# Revit family: M06
name_source: partatom
category: Verbindungsmittel
units: mm (PartAtom-declared; Revit-internal decimal feet)

## family parameters
Arbeitsebenenbasiert = Nein
Beim Laden mit Abzugskörper schneiden = Nein
Gemeinsam genutzt = Nein
Immer vertikal = Nein
OmniClass-Nummer = 23.25.10.27.11.21
OmniClass-Titel = Reinforcement Couplers

## types (10) — shared parameters
Endenbearbeitung 1 = Mit Gewinde
Endenbearbeitung 2 = Mit Gewinde
Hersteller = Stahlwerk Annahütte Max Aicher GmbH Co.KG
M06_Vis = Ja
SW Winkel = 60,00°
Typenbild = M06.png
URL = http//:www.annahuette.com

## per-type parameters (varying)
- M06-ø18: Außendurchmesser=41 mm  [stored 0.134514 ft]; Einfassung Stab 1=50 mm  [stored 0.164042 ft]; Einfassung Stab 2=60 mm  [stored 0.19685 ft]; Gesamtlänge=175 mm; Körper=1,34 kg; M03-Gewicht=1,66 kg; Modell=M06=TR 3105+TR2003; Nenndurchmesser ø=18 mm  [stored 0.0590551 ft]; Pos_TR2003=113 mm; Pos_TR2003_02=143 mm; Pos_TR3014=73 mm; Stabgröße 1=SAS 670 - ø18; Stabgröße 2=SAS 670 - ø18; TR2003-G=0,16 kg; TR2003-L=40 mm  [stored 0.131234 ft]; TR2003-Sw=30 mm  [stored 0.0984252 ft]; TR3013-L0=15 mm  [stored 0.0492126 ft]; TR3013-Lm=45 mm  [stored 0.147638 ft]; TR3013-Lw=60 mm  [stored 0.19685 ft]; TR3013-SW=41 mm  [stored 0.134514 ft]; TR3013-ød=21 mm  [stored 0.0688976 ft]; TR3014-L=145 mm; TR3014-L1=50 mm  [stored 0.164042 ft]; TR3014-L2=45 mm  [stored 0.147638 ft]; TR3014-SW=41 mm  [stored 0.134514 ft]; Typenkommentare=M06-Muffenstoß; minA=30 mm  [stored 0.0984252 ft]
- M06-ø22: Außendurchmesser=46 mm  [stored 0.150919 ft]; Einfassung Stab 1=55 mm  [stored 0.180446 ft]; Einfassung Stab 2=65 mm  [stored 0.213255 ft]; Gesamtlänge=190 mm; Körper=1,78 kg; M03-Gewicht=2,28 kg; Modell=M06=TR 3015+TR2003; Nenndurchmesser ø=22 mm  [stored 0.0721785 ft]; Pos_TR2003=125 mm  [stored 0.410105 ft]; Pos_TR2003_02=155 mm; Pos_TR3014=80 mm  [stored 0.262467 ft]; Stabgröße 1=SAS 670 - ø22; Stabgröße 2=SAS 670 - ø22; TR2003-G=0,25 kg; TR2003-L=45 mm  [stored 0.147638 ft]; TR2003-Sw=36 mm  [stored 0.11811 ft]; TR3013-L0=15 mm  [stored 0.0492126 ft]; TR3013-Lm=50 mm  [stored 0.164042 ft]; TR3013-Lw=65 mm  [stored 0.213255 ft]; TR3013-SW=46 mm  [stored 0.150919 ft]; TR3013-ød=25 mm  [stored 0.082021 ft]; TR3014-L=160 mm; TR3014-L1=55 mm  [stored 0.180446 ft]; TR3014-L2=50 mm  [stored 0.164042 ft]; TR3014-SW=46 mm  [stored 0.150919 ft]; Typenkommentare=M06-Muffenstoß; minA=35 mm  [stored 0.114829 ft]
- M06-ø25: Außendurchmesser=55 mm  [stored 0.180446 ft]; Einfassung Stab 1=60 mm  [stored 0.19685 ft]; Einfassung Stab 2=70 mm  [stored 0.229659 ft]; Gesamtlänge=205 mm; Körper=2,94 kg; M03-Gewicht=3,68 kg; Modell=M06=TR 3015+TR2003; Nenndurchmesser ø=25 mm  [stored 0.082021 ft]; Pos_TR2003=138 mm; Pos_TR2003_02=168 mm; Pos_TR3014=88 mm; Stabgröße 1=SAS 670 - ø25; Stabgröße 2=SAS 670 - ø25; TR2003-G=0,37 kg; TR2003-L=50 mm  [stored 0.164042 ft]; TR2003-Sw=41 mm  [stored 0.134514 ft]; TR3013-L0=15 mm  [stored 0.0492126 ft]; TR3013-Lm=55 mm  [stored 0.180446 ft]; TR3013-Lw=70 mm  [stored 0.229659 ft]; TR3013-SW=55 mm  [stored 0.180446 ft]; TR3013-ød=28 mm  [stored 0.0918635 ft]; TR3014-L=175 mm; TR3014-L1=60 mm  [stored 0.19685 ft]; TR3014-L2=55 mm  [stored 0.180446 ft]; TR3014-SW=55 mm  [stored 0.180446 ft]; Typenkommentare=M06-Muffenstoß; minA=40 mm  [stored 0.131234 ft]
- M06-ø28: Außendurchmesser=50 mm  [stored 0.164042 ft]; Einfassung Stab 1=65 mm  [stored 0.213255 ft]; Einfassung Stab 2=80 mm  [stored 0.262467 ft]; Gesamtlänge=225 mm; Körper=3,74 kg; M03-Gewicht=4,74 kg; Modell=M06=TR 3015+TR2003; Nenndurchmesser ø=28 mm  [stored 0.0918635 ft]; Pos_TR2003=150 mm; Pos_TR2003_02=185 mm; Pos_TR3014=95 mm; Stabgröße 1=SAS 670 - ø28; Stabgröße 2=SAS 670 - ø28; TR2003-G=0,50 kg; TR2003-L=55 mm  [stored 0.180446 ft]; TR2003-Sw=46 mm  [stored 0.150919 ft]; TR3013-L0=20 mm  [stored 0.0656168 ft]; TR3013-Lm=60 mm  [stored 0.19685 ft]; TR3013-Lw=80 mm  [stored 0.262467 ft]; TR3013-SW=60 mm  [stored 0.19685 ft]; TR3013-ød=31 mm  [stored 0.101706 ft]; TR3014-L=190 mm; TR3014-L1=65 mm  [stored 0.213255 ft]; TR3014-L2=60 mm  [stored 0.19685 ft]; TR3014-SW=50 mm  [stored 0.164042 ft]; Typenkommentare=M06-Muffenstoß; minA=45 mm  [stored 0.147638 ft]
- M06-ø30: Außendurchmesser=65 mm  [stored 0.213255 ft]; Einfassung Stab 1=70 mm  [stored 0.229659 ft]; Einfassung Stab 2=95 mm; Gesamtlänge=260 mm; Körper=5,11 kg; M03-Gewicht=6,45 kg; Modell=M06=TR 3015+TR2003; Nenndurchmesser ø=30 mm  [stored 0.0984252 ft]; Pos_TR2003=168 mm; Pos_TR2003_02=213 mm; Pos_TR3014=108 mm; Stabgröße 1=SAS 670 - ø30; Stabgröße 2=SAS 670 - ø30; TR2003-G=0,67 kg; TR2003-L=60 mm  [stored 0.19685 ft]; TR2003-Sw=50 mm  [stored 0.164042 ft]; TR3013-L0=25 mm  [stored 0.082021 ft]; TR3013-Lm=70 mm  [stored 0.229659 ft]; TR3013-Lw=95 mm; TR3013-SW=65 mm  [stored 0.213255 ft]; TR3013-ød=33 mm; TR3014-L=215 mm; TR3014-L1=70 mm  [stored 0.229659 ft]; TR3014-L2=65 mm  [stored 0.213255 ft]; TR3014-SW=65 mm  [stored 0.213255 ft]; Typenkommentare=M06-Muffenstoß; minA=50 mm  [stored 0.164042 ft]
- M06-ø35: Außendurchmesser=80 mm  [stored 0.262467 ft]; Einfassung Stab 1=75 mm; Einfassung Stab 2=100 mm  [stored 0.328084 ft]; Gesamtlänge=275 mm; Körper=8,27 kg; M03-Gewicht=9,83 kg; Modell=M06=TR 3015+TR2003; Nenndurchmesser ø=35 mm  [stored 0.114829 ft]; Pos_TR2003=180 mm; Pos_TR2003_02=225 mm; Pos_TR3014=115 mm  [stored 0.377297 ft]; Stabgröße 1=SAS 670 - ø35; Stabgröße 2=SAS 670 - ø35; TR2003-G=0,78 kg; TR2003-L=65 mm  [stored 0.213255 ft]; TR2003-Sw=55 mm  [stored 0.180446 ft]; TR3013-L0=25 mm  [stored 0.082021 ft]; TR3013-Lm=75 mm; TR3013-Lw=100 mm  [stored 0.328084 ft]; TR3013-SW=80 mm  [stored 0.262467 ft]; TR3013-ød=38 mm  [stored 0.124672 ft]; TR3014-L=230 mm; TR3014-L1=75 mm; TR3014-L2=75 mm; TR3014-SW=80 mm  [stored 0.262467 ft]; Typenkommentare=M06-Muffenstoß; minA=55 mm  [stored 0.180446 ft]
- M06-ø43: Außendurchmesser=90 mm  [stored 0.295276 ft]; Einfassung Stab 1=100 mm  [stored 0.328084 ft]; Einfassung Stab 2=115 mm  [stored 0.377297 ft]; Gesamtlänge=335 mm; Körper=15,14 kg; M03-Gewicht=18,34 kg; Modell=M06=TR 3015+TR2003; Nenndurchmesser ø=43 mm  [stored 0.141076 ft]; Pos_TR2003=220 mm; Pos_TR2003_02=275 mm; Pos_TR3014=140 mm; Stabgröße 1=SAS 670 - ø43; Stabgröße 2=SAS 670 - ø43; TR2003-G=1,60 kg; TR2003-L=80 mm  [stored 0.262467 ft]; TR2003-Sw=70 mm  [stored 0.229659 ft]; TR3013-L0=25 mm  [stored 0.082021 ft]; TR3013-Lm=90 mm  [stored 0.295276 ft]; TR3013-Lw=115 mm  [stored 0.377297 ft]; TR3013-SW=90 mm  [stored 0.295276 ft]; TR3013-ød=46 mm  [stored 0.150919 ft]; TR3014-L=280 mm; TR3014-L1=100 mm  [stored 0.328084 ft]; TR3014-L2=90 mm  [stored 0.295276 ft]; TR3014-SW=90 mm  [stored 0.295276 ft]; Typenkommentare=M06-Muffenstoß; minA=60 mm  [stored 0.19685 ft]
- M06-ø50: Außendurchmesser=100 mm  [stored 0.328084 ft]; Einfassung Stab 1=100 mm  [stored 0.328084 ft]; Einfassung Stab 2=125 mm  [stored 0.410105 ft]; Gesamtlänge=350 mm; Körper=19,04 kg; M03-Gewicht=23,58 kg; Modell=M06=TR 3015+TR2003; Nenndurchmesser ø=50 mm  [stored 0.164042 ft]; Pos_TR2003=240 mm; Pos_TR2003_02=290 mm; Pos_TR3014=150 mm; Stabgröße 1=SAS 670 - ø50; Stabgröße 2=SAS 670 - ø50; TR2003-G=2,27 kg; TR2003-L=90 mm  [stored 0.295276 ft]; TR2003-Sw=80 mm  [stored 0.262467 ft]; TR3013-L0=25 mm  [stored 0.082021 ft]; TR3013-Lm=100 mm  [stored 0.328084 ft]; TR3013-Lw=125 mm  [stored 0.410105 ft]; TR3013-SW=75 mm; TR3013-ød=53 mm; TR3014-L=300 mm; TR3014-L1=100 mm  [stored 0.328084 ft]; TR3014-L2=100 mm  [stored 0.328084 ft]; TR3014-SW=100 mm  [stored 0.328084 ft]; Typenkommentare=M06-Muffenstoß; minA=75 mm
- M06-ø57,5: Außendurchmesser=100 mm  [stored 0.328084 ft]; Einfassung Stab 1=125 mm  [stored 0.410105 ft]; Einfassung Stab 2=135 mm  [stored 0.442913 ft]; Gesamtlänge=405 mm; Körper=24,46 kg; M03-Gewicht=31,88 kg; Modell=M06=TR 3015+TR2006; Nenndurchmesser ø=58 mm; Pos_TR2003=273 mm; Pos_TR2003_02=333 mm; Pos_TR3014=173 mm; Stabgröße 1=SAS 670 - ø57,5; Stabgröße 2=SAS 670 - ø57,5; TR2003-G=3,71 kg; TR2003-L=100 mm  [stored 0.328084 ft]; TR2003-Sw=90 mm  [stored 0.295276 ft]; TR3013-L0=35 mm  [stored 0.114829 ft]; TR3013-Lm=100 mm  [stored 0.328084 ft]; TR3013-Lw=135 mm  [stored 0.442913 ft]; TR3013-SW=100 mm  [stored 0.328084 ft]; TR3013-ød=61 mm; TR3014-L=345 mm; TR3014-L1=125 mm  [stored 0.410105 ft]; TR3014-L2=100 mm  [stored 0.328084 ft]; TR3014-SW=100 mm  [stored 0.328084 ft]; Typenkommentare=M06-Muffenstoß; minA=75 mm
- M06-ø63,5: Außendurchmesser=100 mm  [stored 0.328084 ft]; Einfassung Stab 1=140 mm; Einfassung Stab 2=140 mm; Gesamtlänge=425 mm; Körper=21,56 kg; M03-Gewicht=32,46 kg; Modell=M06=TR 3015+TR2003; Nenndurchmesser ø=43 mm  [stored 0.141076 ft]; Pos_TR2003=298 mm; Pos_TR2003_02=358 mm; Pos_TR3014=183 mm; Stabgröße 1=SAS 670 - ø63,5; Stabgröße 2=SAS 670 - ø63,5; TR2003-G=5,45 kg; TR2003-L=115 mm  [stored 0.377297 ft]; TR2003-Sw=100 mm  [stored 0.328084 ft]; TR3013-L0=35 mm  [stored 0.114829 ft]; TR3013-Lm=105 mm  [stored 0.344488 ft]; TR3013-Lw=140 mm; TR3013-SW=100 mm  [stored 0.328084 ft]; TR3013-ød=46 mm  [stored 0.150919 ft]; TR3014-L=365 mm; TR3014-L1=140 mm; TR3014-L2=105 mm  [stored 0.344488 ft]; TR3014-SW=100 mm  [stored 0.328084 ft]; Typenkommentare=M06 - Muffenstoß; minA=80 mm  [stored 0.262467 ft]

note: column(s) folded — value = type name in every type: Beschreibung

note: [stored X ft] marks values corroborated as IEEE doubles in the binary element streams (Revit-internal decimal feet)
